# Revit family: Clevertronics_ARGO-600-EM-AUB03520120001
name_source: partatom
category: Lighting Fixtures
units: mm (PartAtom-declared; Revit-internal decimal feet)

## family parameters
Cut with Voids When Loaded = No
Host = Face
Light Source = Yes
Part Type = Normal
Room Calculation Point = No
Round Connector Dimension = Use Diameter
Shared = No

## types (1)
- ARGO-600-EM
    Apparent Load = 20 VA
    Clevertronics_240V Driver = 1330086-A - 240V Driver
    Clevertronics_240V LED Strip = 8002848 - LED Strip
    Clevertronics_AS2293 Classification = C0=D40 C90=D25
    Clevertronics_Annotation Size = 0 mm  [stored 0 ft]
    Clevertronics_Applicable Standards = AS/NZS3820, CISPR15, AS/NZS2293.3
    Clevertronics_Battery = 3.2V 3000mAh
    Clevertronics_Battery Type = Lithium Iron Phosphate
    Clevertronics_Charger Method = Intelligent current limited constant voltage
    Clevertronics_Construction = Polycarbonate Base and Diffuser with Captive Stainless-Steel Clips (SS301)
    Clevertronics_Diffuser = Polycarbonate
    Clevertronics_Driver/Ballast = LED Driver – 20w Stallion
    Clevertronics_Emergency Driver = ELIFE-X-LI-CKIT-2LED-SL-NP - Driver
    Clevertronics_Height = 88 mm  [stored 0.288714 ft]
    Clevertronics_IK Rating = IK08
    Clevertronics_IP Rating = IP65
    Clevertronics_Length = 655 mm  [stored 2.14895 ft]
    Clevertronics_MIC Number = AUB03520120001
    Clevertronics_Material = Clevertronics_Plycarbonate Base
    Clevertronics_Mounting = Surface mount
    Clevertronics_Operating Mode = Sustained
    Clevertronics_Operating Temperature = 0˚C to 40˚C
    Clevertronics_Operating Voltage = 240V AC; 50Hz
    Clevertronics_Power Consumption = 20W
    Clevertronics_Product Description = Economy ARGO 600mm LED Weatherproof Batten with Switchable Colour
    Clevertronics_Replacement Battery = 1560150 - Battery
    Clevertronics_Total Lumen Output = 2150lm
    Clevertronics_Weight = 1.5 kg
    Clevertronics_Width = 121 mm  [stored 0.396982 ft]
    Color Filter = 16777215
    Default Elevation = 1200 mm
    Description = Economy ARGO 600mm LED Weatherproof Batten with Switchable Colour
    Dimming Lamp Color Temperature Shift = <None>
    Lamp = Dual LED strip module, 3,000K warm white, 5,700K cool white, 
50,000h life [L70/B50 Ta 40°C], Ra>80
    Manufacturer = Clevertronics
    Model = ARGO-600-EM
    Photometric Web File = ARGO-600-EM_IESR_E_693-7_20200701 (1).ies
    Tilt Angle = -90.00°

note: [stored X ft] marks values corroborated as IEEE doubles in the binary element streams (Revit-internal decimal feet)

## geometry (parser evidence)
native form markers: Blend x2, Sweep x2
no freeform markers — native parametric forms only
